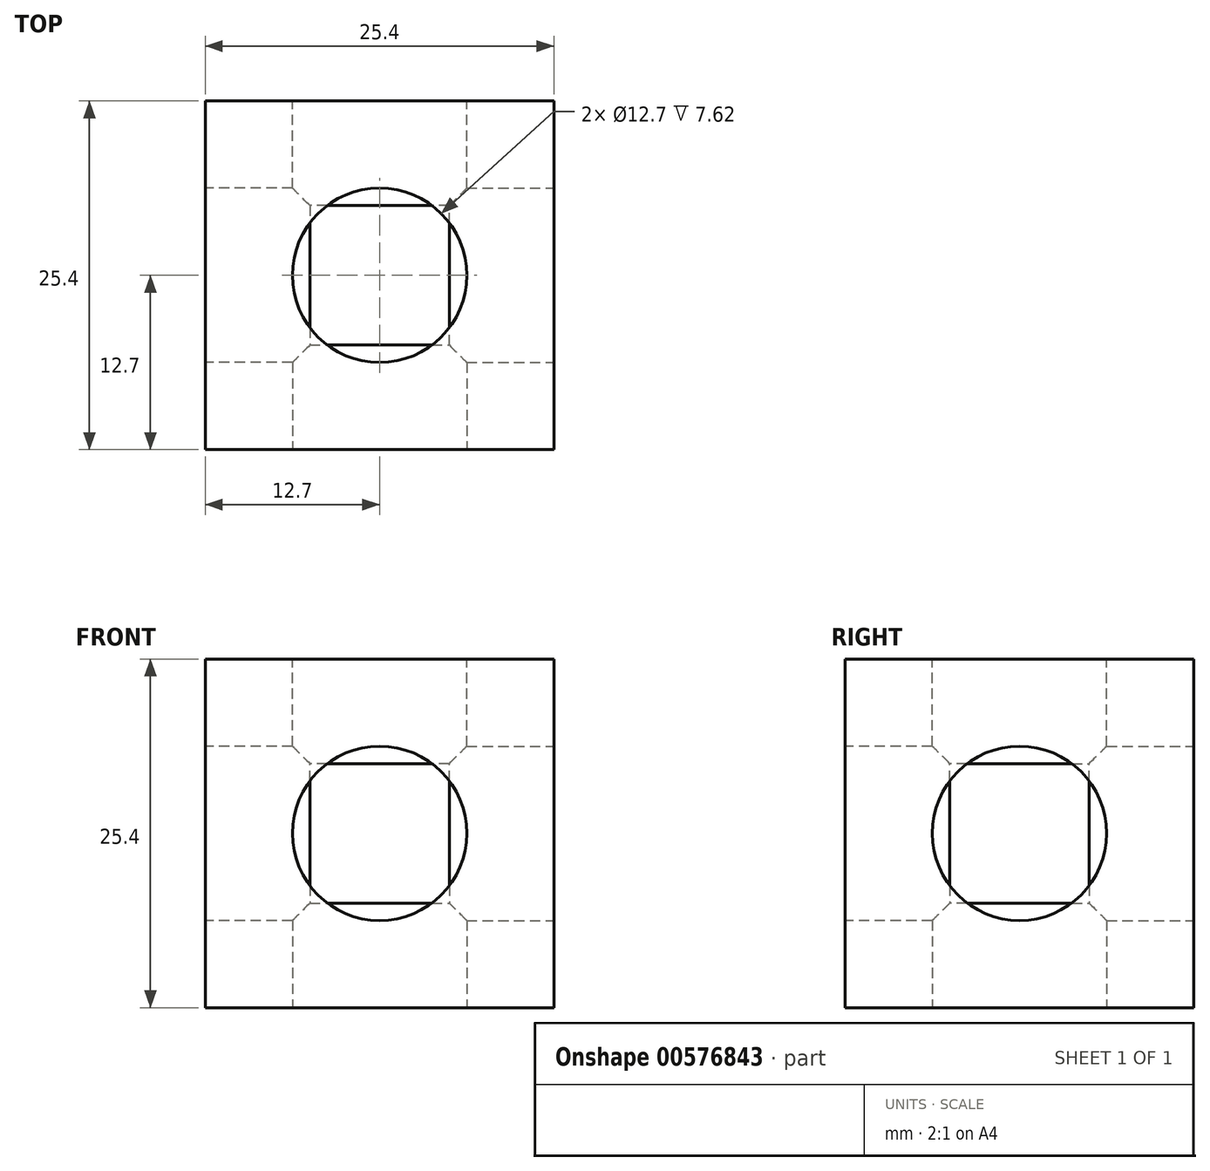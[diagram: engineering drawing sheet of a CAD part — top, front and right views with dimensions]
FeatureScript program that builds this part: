
annotation { "Feature Type Name" : "Feature", "Feature Type Description" : "" }
export const myFeature = defineFeature(function(context is Context, id is Id, definition is map)
    precondition{}
    {
        {
            var Q0;
            Q0=qCreatedBy(makeId("Front.planeOp"),FACE);
            var sketch = newSketch(context, id + "F0", { "sketchPlane" : qUnion([Q0])});
            skLineSegment(sketch, "E0.bottom", {"start": v(-12.7, 12.7) * mm, "end": v(12.7, 12.7) * mm});
            skLineSegment(sketch, "E0.top", {"start": v(-12.7, -12.7) * mm, "end": v(12.7, -12.7) * mm});
            skLineSegment(sketch, "E0.left", {"start": v(-12.7, 12.7) * mm, "end": v(-12.7, -12.7) * mm});
            skLineSegment(sketch, "E0.right", {"start": v(12.7, 12.7) * mm, "end": v(12.7, -12.7) * mm});
            skPoint(sketch, "E0.middle", {"position": v(0, 0) * mm});
            skSolve(sketch);
        }
        {
            var Q0;
            Q0 = qSketchRegion(id + "F0", true);
            extrude(context, id + "F1", {"entities" : qUnion([Q0]), "depth" : 25.4 * mm, "offsetDistance" : 25.4 * mm});
        }
        {
            var Q0;
            Q0=makeQuery(id+"F1.opExtrude","CAP_FACE",FACE,{"disambiguationData":[OSD([sQuery(id+"F0.wireOp",EDGE,"E0.bottom"),sQuery(id+"F0.wireOp",EDGE,"E0.top"),sQuery(id+"F0.wireOp",EDGE,"E0.left"),sQuery(id+"F0.wireOp",EDGE,"E0.right")])],"isStart":false});
            var sketch = newSketch(context, id + "F2", { "sketchPlane" : qUnion([Q0])});
            skCircle(sketch, "E1", {"center": v(0, 0) * mm, "radius": 6.35 * mm});
            skSolve(sketch);
        }
        {
            var Q0;
            Q0 = qSketchRegion(id + "F2", true);
            extrude(context, id + "F3", {"entities" : qUnion([Q0]), "operationType" : NewBodyOperationType.REMOVE, "oppositeDirection" : true, "depth" : 7.62 * mm, "offsetDistance" : 25.4 * mm});
        }
        {
            var Q0;
            Q0=makeQuery(id+"F1.opExtrude","CAP_FACE",FACE,{"disambiguationData":[OSD([sQuery(id+"F0.wireOp",EDGE,"E0.bottom"),sQuery(id+"F0.wireOp",EDGE,"E0.top"),sQuery(id+"F0.wireOp",EDGE,"E0.left"),sQuery(id+"F0.wireOp",EDGE,"E0.right")])],"isStart":true});
            var sketch = newSketch(context, id + "F4", { "sketchPlane" : qUnion([Q0])});
            skCircle(sketch, "E2", {"center": v(0, 0) * mm, "radius": 6.35 * mm});
            skSolve(sketch);
        }
        {
            var Q0;
            Q0 = qSketchRegion(id + "F4", true);
            var Q1;
            Q1 = qSketchRegion(id + "F6", true);
            extrude(context, id + "F5", {"entities" : qUnion([Q0, Q1]), "operationType" : NewBodyOperationType.REMOVE, "oppositeDirection" : true, "depth" : 7.62 * mm, "offsetDistance" : 25.4 * mm});
        }
        {
            var Q0;
            Q0=makeQuery(id+"F1.opExtrude","SWEPT_FACE",FACE,{"disambiguationData":[OSD([sQuery(id+"F0.wireOp",EDGE,"E0.right")])]});
            var sketch = newSketch(context, id + "F6", { "sketchPlane" : qUnion([Q0])});
            skCircle(sketch, "E3", {"center": v(-12.7, 0) * mm, "radius": 6.35 * mm});
            skSolve(sketch);
        }
        {
            var Q0;
            Q0 = qSketchRegion(id + "F6", true);
            extrude(context, id + "F7", {"entities" : qUnion([Q0]), "operationType" : NewBodyOperationType.REMOVE, "oppositeDirection" : true, "depth" : 7.62 * mm, "offsetDistance" : 25.4 * mm});
        }
        {
            var Q0;
            Q0=makeQuery(id+"F1.opExtrude","SWEPT_FACE",FACE,{"disambiguationData":[OSD([sQuery(id+"F0.wireOp",EDGE,"E0.left")])]});
            var sketch = newSketch(context, id + "F8", { "sketchPlane" : qUnion([Q0])});
            skCircle(sketch, "E4", {"center": v(12.7, 0) * mm, "radius": 6.35 * mm});
            skSolve(sketch);
        }
        {
            var Q0;
            Q0 = qSketchRegion(id + "F8", true);
            extrude(context, id + "F9", {"entities" : qUnion([Q0]), "operationType" : NewBodyOperationType.REMOVE, "oppositeDirection" : true, "depth" : 7.62 * mm, "offsetDistance" : 25.4 * mm});
        }
        {
            var Q0;
            Q0=makeQuery(id+"F1.opExtrude","SWEPT_FACE",FACE,{"disambiguationData":[OSD([sQuery(id+"F0.wireOp",EDGE,"E0.bottom")])]});
            var sketch = newSketch(context, id + "F10", { "sketchPlane" : qUnion([Q0])});
            skCircle(sketch, "E5", {"center": v(0, -12.7) * mm, "radius": 6.35 * mm});
            skSolve(sketch);
        }
        {
            var Q0;
            Q0 = qSketchRegion(id + "F10", true);
            extrude(context, id + "F11", {"entities" : qUnion([Q0]), "operationType" : NewBodyOperationType.REMOVE, "oppositeDirection" : true, "depth" : 7.62 * mm, "offsetDistance" : 25.4 * mm});
        }
        {
            var Q0;
            Q0=makeQuery(id+"F1.opExtrude","SWEPT_FACE",FACE,{"disambiguationData":[OSD([sQuery(id+"F0.wireOp",EDGE,"E0.top")])]});
            var sketch = newSketch(context, id + "F12", { "sketchPlane" : qUnion([Q0])});
            skCircle(sketch, "E6", {"center": v(0, 12.7) * mm, "radius": 6.35 * mm});
            skSolve(sketch);
        }
        {
            var Q0;
            Q0 = qSketchRegion(id + "F12", true);
            extrude(context, id + "F13", {"entities" : qUnion([Q0]), "operationType" : NewBodyOperationType.REMOVE, "oppositeDirection" : true, "depth" : 7.62 * mm, "offsetDistance" : 25.4 * mm});
        }
    });
